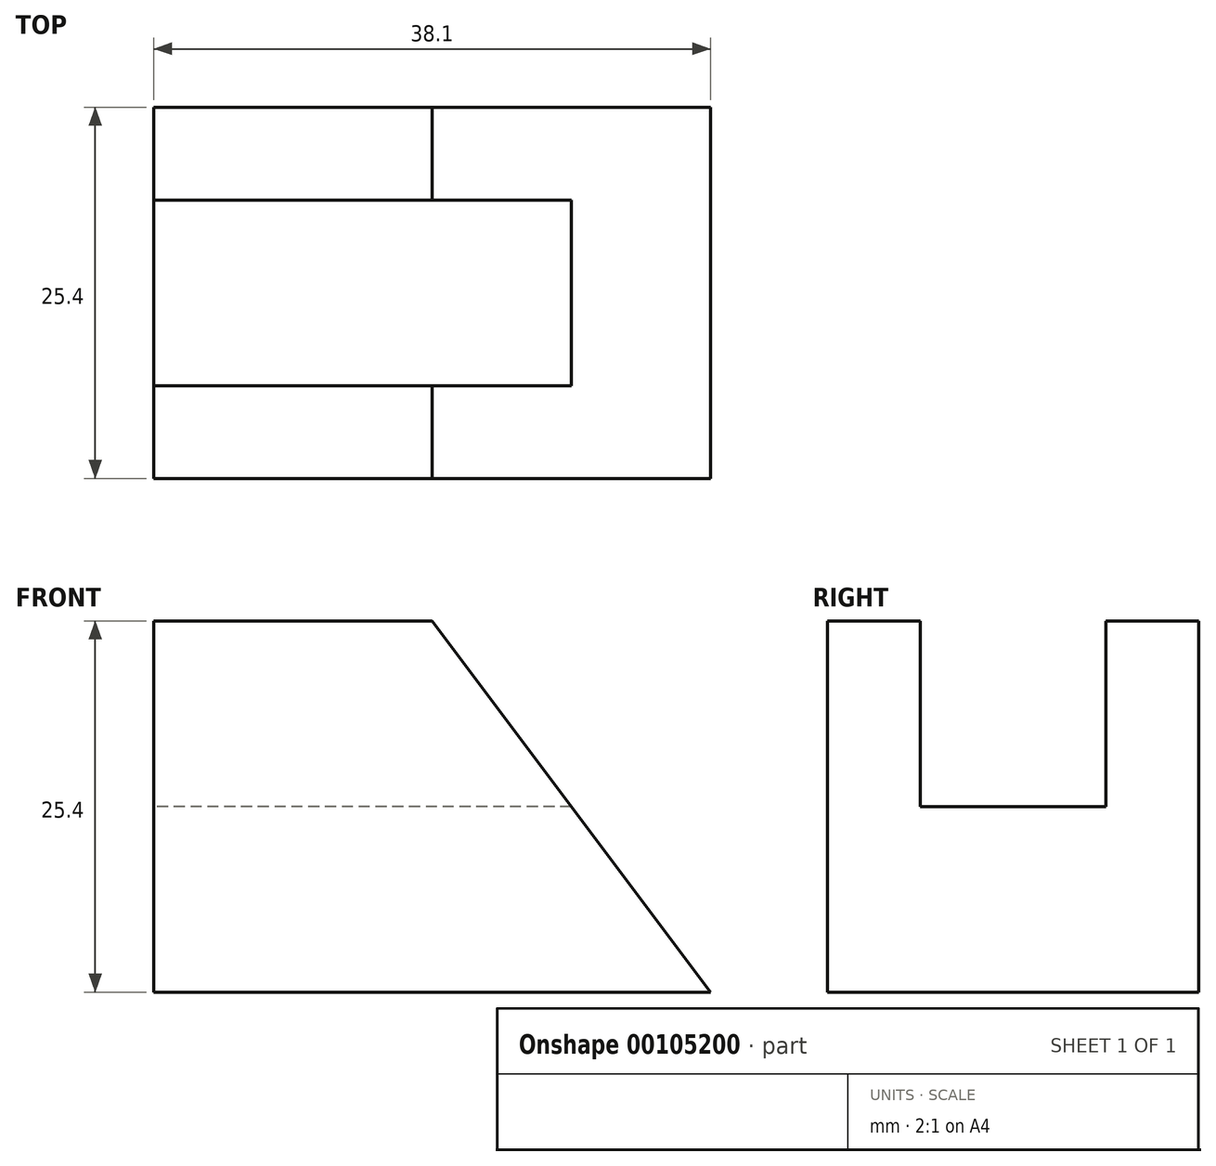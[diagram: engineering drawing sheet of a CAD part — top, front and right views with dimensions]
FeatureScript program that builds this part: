
annotation { "Feature Type Name" : "Feature", "Feature Type Description" : "" }
export const myFeature = defineFeature(function(context is Context, id is Id, definition is map)
    precondition{}
    {
        {
            var Q0;
            Q0=qCreatedBy(makeId("Front.planeOp"),FACE);
            var sketch = newSketch(context, id + "F0", { "sketchPlane" : qUnion([Q0])});
            skLineSegment(sketch, "E0", {"start": v(0, 0) * mm, "end": v(0, 25.4) * mm});
            skLineSegment(sketch, "E1", {"start": v(0, 25.4) * mm, "end": v(19.05, 25.4) * mm});
            skLineSegment(sketch, "E2", {"start": v(19.05, 25.4) * mm, "end": v(38.1, 0) * mm});
            skLineSegment(sketch, "E3", {"start": v(38.1, 0) * mm, "end": v(0, 0) * mm});
            skSolve(sketch);
        }
        {
            var Q0;
            Q0 = qSketchRegion(id + "F0", true);
            extrude(context, id + "F1", {"entities" : qUnion([Q0]), "endBound" : BoundingType.SYMMETRIC, "depth" : 25.4 * mm});
        }
        {
            var Q0;
            Q0=qCreatedBy(makeId("Right.planeOp"),FACE);
            var sketch = newSketch(context, id + "F2", { "sketchPlane" : qUnion([Q0])});
            skLineSegment(sketch, "E4.bottom", {"start": v(6.35, 25.4) * mm, "end": v(-6.35, 25.4) * mm});
            skLineSegment(sketch, "E4.top", {"start": v(6.35, 12.7) * mm, "end": v(-6.35, 12.7) * mm});
            skLineSegment(sketch, "E4.left", {"start": v(6.35, 25.4) * mm, "end": v(6.35, 12.7) * mm});
            skLineSegment(sketch, "E4.right", {"start": v(-6.35, 25.4) * mm, "end": v(-6.35, 12.7) * mm});
            skSolve(sketch);
        }
        {
            var Q0;
            Q0 = qSketchRegion(id + "F2", true);
            extrude(context, id + "F3", {"entities" : qUnion([Q0]), "operationType" : NewBodyOperationType.REMOVE, "endBound" : BoundingType.THROUGH_ALL, "depth" : 25.4 * mm});
        }
    });
